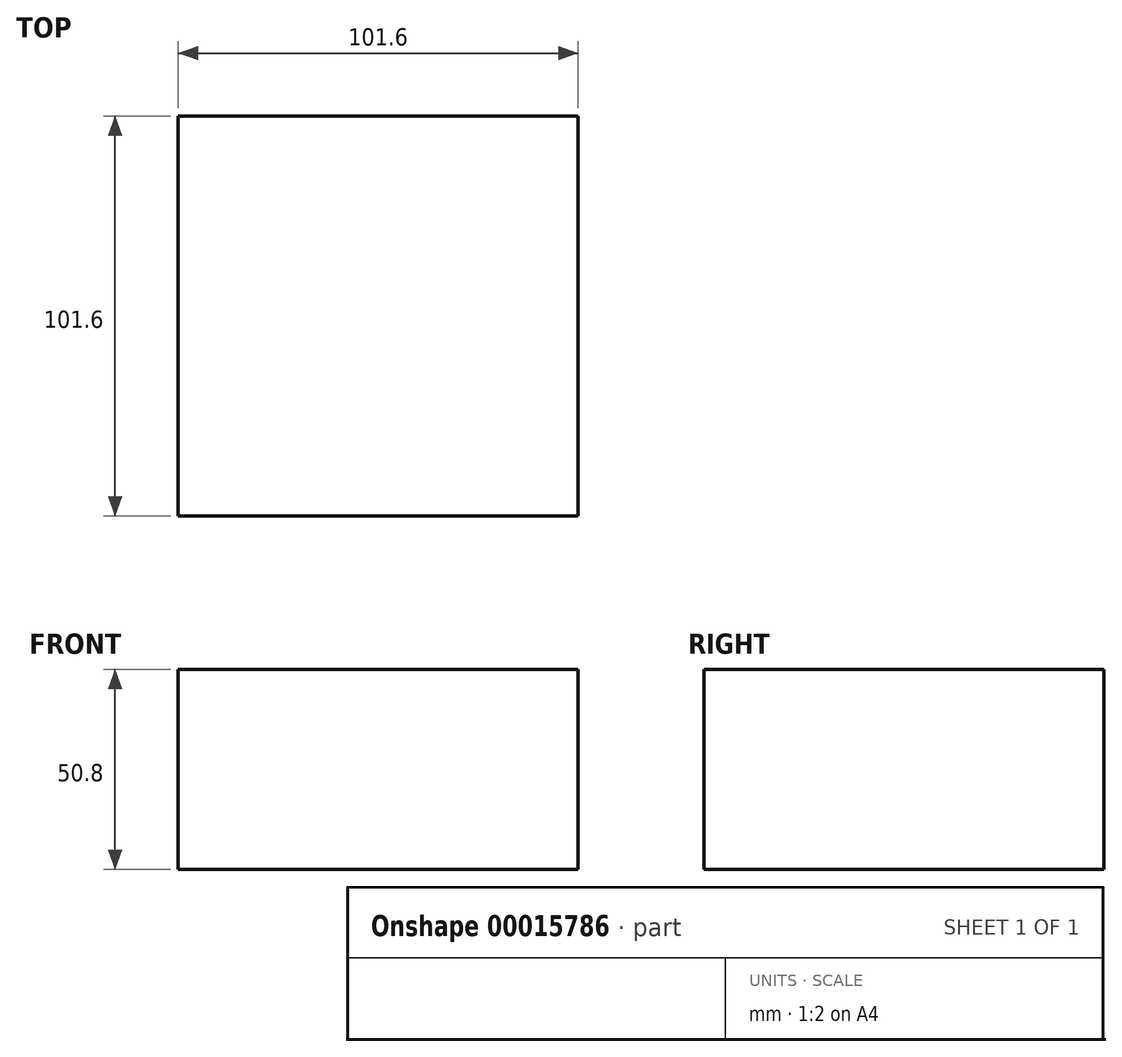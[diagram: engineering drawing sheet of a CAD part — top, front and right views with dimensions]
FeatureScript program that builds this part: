
annotation { "Feature Type Name" : "Feature", "Feature Type Description" : "" }
export const myFeature = defineFeature(function(context is Context, id is Id, definition is map)
    precondition{}
    {
        {
            var Q0;
            Q0=qCreatedBy(makeId("Top.planeOp"),FACE);
            var sketch = newSketch(context, id + "F0", { "sketchPlane" : qUnion([Q0])});
            skLineSegment(sketch, "E0.bottom", {"start": v(0, 0) * mm, "end": v(101.6, 0) * mm});
            skLineSegment(sketch, "E0.top", {"start": v(0, -101.6) * mm, "end": v(101.6, -101.6) * mm});
            skLineSegment(sketch, "E0.left", {"start": v(0, 0) * mm, "end": v(0, -101.6) * mm});
            skLineSegment(sketch, "E0.right", {"start": v(101.6, 0) * mm, "end": v(101.6, -101.6) * mm});
            skSolve(sketch);
        }
        {
            var Q0;
            Q0=qSketchRegion(id+"F0",true);
            extrude(context, id + "F1", {"entities" : qUnion([Q0]), "depth" : 50.8 * mm});
        }
    });
